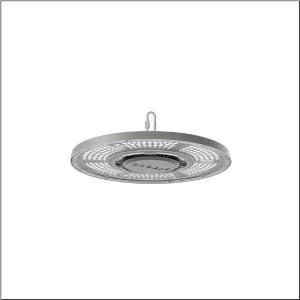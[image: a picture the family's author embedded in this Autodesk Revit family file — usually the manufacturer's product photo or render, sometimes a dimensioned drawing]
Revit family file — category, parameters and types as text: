
# Revit family: highbay_31-s_51hc417a4jmb
name_source: partatom
category: Lighting Fixtures
units: mm (PartAtom-declared; Revit-internal decimal feet)

## family parameters
Cut with Voids When Loaded = No
Host = Face
Light Source = No
Part Type = Normal
Room Calculation Point = No
Round Connector Dimension = Use Diameter
Shared = No

## types (1)
- Highbay 31-S (1 x LED, 20000 lm, 134 W, 4000K)
    Apparent Load = 134 VA
    CIE Flux Codes = 95 98 100 100 100
    Color Rendering = 80
    Color Temperature = 4000K
    Default Elevation = 1800 mm
    Description = Highbay 31-S, LED high bay luminaire, primary light control with lens, of PC, primary optical cover: cover panel, of PC, transparent, light emission: direct distribution, primary light characteristic: rotationally symmetric, installation type: suspended mounting, surface-mounted, LED, rated luminous flux: 20.000lm, luminous efficacy: 150lm/W, light colour: 840, colour temperature: 4000K, control gear: ECG, with cable, 3x 1.0mm², free wire ends, mains connection: 220..240V, AC/DC, 0/50..60Hz, cable length: 1,5m, rated input power: 134W, housing, rotationally symmetric, of diecast aluminium, powder-coated, grey aluminium (RAL 9007), with hook on luminaire side, incl. screw, diameter: 339mm, protection rating (complete): IP65, insulation class (complete): insulation class I (protective earthing), certification: CE, ENEC, UKCA, protection symbol: D, impact resistance: IK08, permissible operating ambient temperature: -30..+45°C, standard: EN 60598-2-22, EN 60598, corresponds to IFS (International Featured Standards) requirements for safety and quality in the food industry, packaging unit: 1 piece
    Height = 141 mm
    Lamp = 1 x LED
    Lamp Light Flux = 20000 lm
    Lamp Power = 134 W
    Lamp count = 1
    Length = 339 mm
    Luminous efficacy = 149 lm/W
    Manufacturer = Siteco
    ModVariant = No
    Model = 51HC417A4JMB
    Mounting Place = Ceiling
    Mounting Type = Pendant
    Number of Poles = 1
    OnlyDefault = Yes
    Power Factor = 1
    Product Name = Highbay 31-S
    Product group = LED high bay luminaire
    ProductGroupID = 903
    Protection Class = Protection class I
    Protection Degree = IP 65
    RLX_Detail_Level = 1
    RLX_Emergency_Light_Flux = 0 lm
    RLX_Emergency_Type = 0
    RLX_Emergency_Type_DB = No
    RlxData = <blob elided: 106805 chars, md5=25f32dbd>
    Socket = socket
    Standby Power = 0 W
    System Light Flux = 20000 lm
    System Power = 134 W
    Type Comments = Product without accessories
    Type Image = l_1007237.jpg
    URL = http://relux.com
    VarID = ---
    Voltage = 0 V
    Weight = 0.00 kg
    Width = 0 mm  [stored 0 ft]

note: [stored X ft] marks values corroborated as IEEE doubles in the binary element streams (Revit-internal decimal feet)

## geometry (parser evidence)
native form markers: Blend x4, Sweep x11
no freeform markers — native parametric forms only
